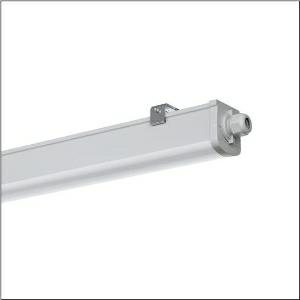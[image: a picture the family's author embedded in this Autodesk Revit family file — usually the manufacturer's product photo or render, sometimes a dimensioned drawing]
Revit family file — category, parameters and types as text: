
# Revit family: monsun_r__31_51fa207p430b_b845
name_source: partatom
category: Lighting Fixtures
units: mm (PartAtom-declared; Revit-internal decimal feet)

## family parameters
Cut with Voids When Loaded = No
Host = Face
Light Source = No
Part Type = Normal
Room Calculation Point = No
Round Connector Dimension = Use Diameter
Shared = No

## types (1)
- Monsun® 31 (1 x LED, 3800 lm, 28 W, 4000K)
    Apparent Load = 28 VA
    CIE Flux Codes = 42 72 91 92 100
    Color Rendering = 80
    Color Temperature = 4000K
    Default Elevation = 1800 mm
    Description = Monsun® 31, damp-proof luminaire, primary optical cover: diffuser, of PC, frosted, light emission: direct distribution, primary light characteristic: symmetric, installation type: surface-mounted, LED, rated luminous flux: 3.800lm, luminous efficacy: 136lm/W, light colour: 840, colour temperature: 4000K, control gear: ON/OFF, with terminal, 3+1-pole, max. 2.5mm², through-wiring: 3x 2.5mm² + 1x 1.5mm², mains connection: 220..240V, AC, 50/60Hz, rated input power: 28W, housing, luminaire housing, of PC, light grey (RAL 7035), length: 1.458mm, width: 68mm, height: 76mm, protection rating (complete): IP66, insulation class (complete): insulation class II (safety insulation), certification: CE, ENEC, UKCA, protection symbol: D, impact resistance: IK08, permissible operating ambient temperature: -20..+40°C, corresponds to IFS (International Featured Standards) requirements for safety and quality in the food industry, contact your sales advisor before using the luminaires in applications with unclear chemical exposure, large temperature fluctuations or condensation-forming humidity, packaging unit: 1 piece
    Height = 77 mm
    Lamp = 1 x LED
    Lamp Light Flux = 3800 lm
    Lamp Power = 28 W
    Lamp count = 1
    Length = 1518 mm
    Luminous efficacy = 136 lm/W
    Manufacturer = Siteco
    ModVariant = No
    Model = 51FA207P430B
    Mounting Place = Ceiling
    Mounting Type = Surface mounted
    Number of Poles = 1
    OnlyDefault = Yes
    Power Factor = 1
    Product Name = Monsun® 31
    Product group = damp-proof luminaire
    ProductGroupID = 300
    Protection Class = Protection class II
    Protection Degree = IP 66
    RLX_Detail_Level = 1
    RLX_Emergency_Light_Flux = 0 lm
    RLX_Emergency_Type = 0
    RLX_Emergency_Type_DB = No
    RlxData = <blob elided: 33245 chars, md5=fe5b178e>
    Socket = socket
    Standby Power = 0 W
    System Light Flux = 3800 lm
    System Power = 28 W
    Type Comments = Product without accessories
    Type Image = l_1006174.jpg
    URL = http://relux.com
    VarID = ---
    Voltage = 0 V
    Weight = 0.00 kg
    Width = 69 mm

## geometry (parser evidence)
native form markers: Blend x4, Sweep x13
no freeform markers — native parametric forms only
